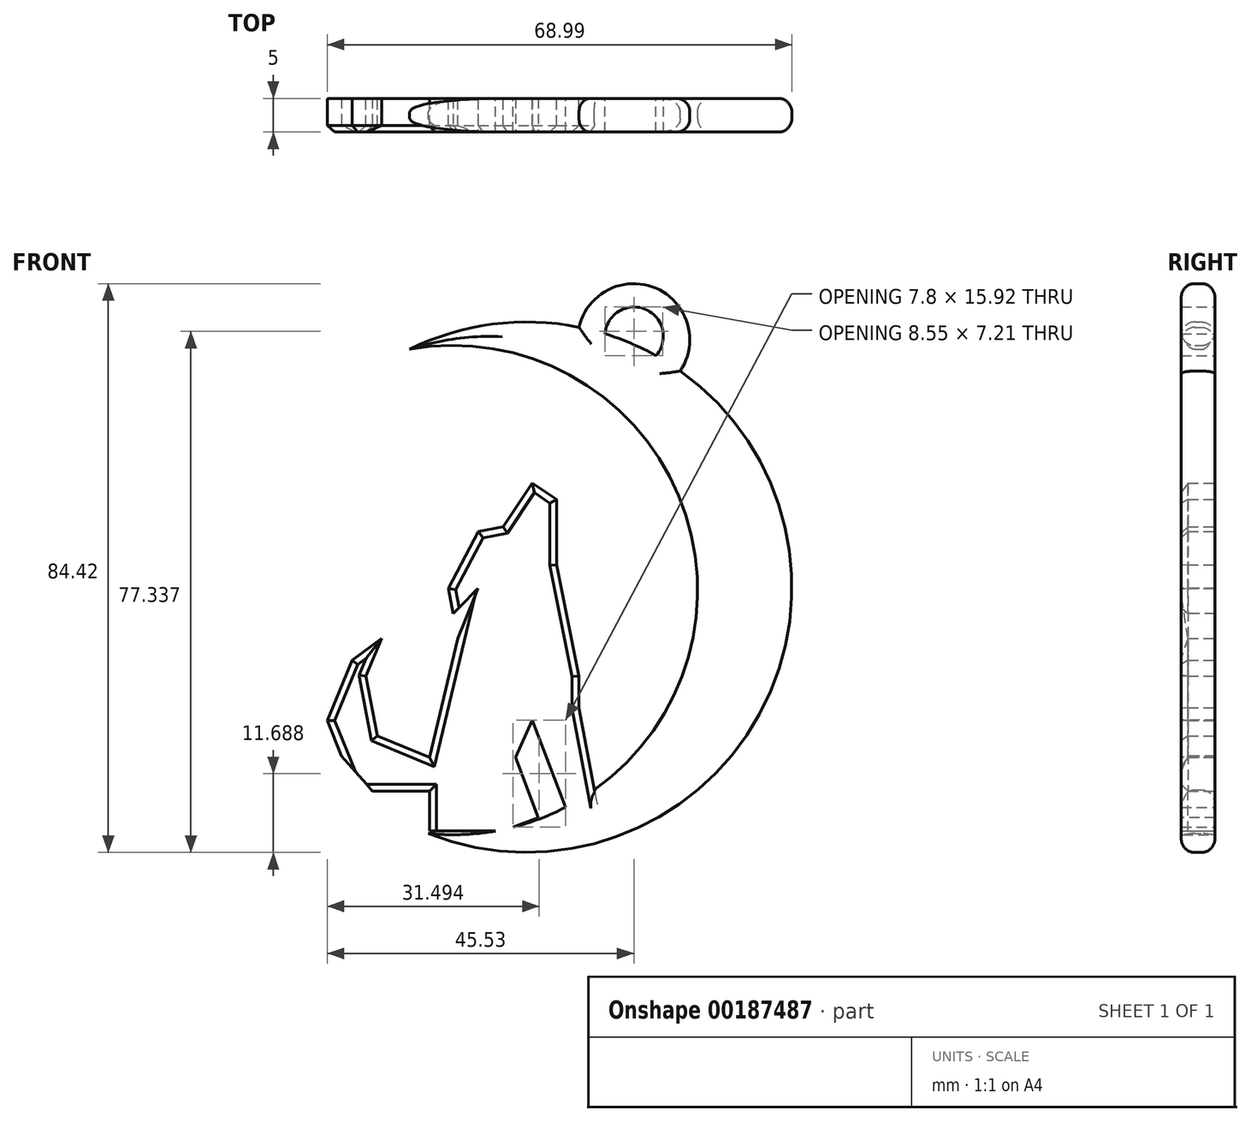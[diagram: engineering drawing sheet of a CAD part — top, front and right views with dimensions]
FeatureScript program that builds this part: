
annotation { "Feature Type Name" : "Feature", "Feature Type Description" : "" }
export const myFeature = defineFeature(function(context is Context, id is Id, definition is map)
    precondition{}
    {
        {
            var Q0;
            Q0=qCreatedBy(makeId("Front.planeOp"),FACE);
            var sketch = newSketch(context, id + "F0", { "sketchPlane" : qUnion([Q0])});
            skArc(sketch, "E0", {"start": v(-15.44, -36.36) * mm, "mid": v(33.72, -18.63) * mm, "end": v(21.95, 32.3) * mm});
            skArc(sketch, "E1", {"start": v(-15.44, -36.36) * mm, "mid": v(24.5, 1.2) * mm, "end": v(-18.25, 35.51) * mm});
            skArc(sketch, "E2", {"start": v(21.95, 32.3) * mm, "mid": v(18.35, 44.58) * mm, "end": v(6.93, 38.8) * mm});
            skArc(sketch, "E3", {"start": v(18.35, 34.57) * mm, "mid": v(16.81, 41.44) * mm, "end": v(10.78, 37.81) * mm});
            skPoint(sketch, "E3.startSnap0", {"position": v(18.35, 44.58) * mm});
            skArc(sketch, "E4.trimOffspring", {"start": v(6.93, 38.8) * mm, "mid": v(-5.93, 39.24) * mm, "end": v(-18.25, 35.51) * mm});
            skArc(sketch, "E5.trimOffspring", {"start": v(18.35, 34.57) * mm, "mid": v(14.65, 36.4) * mm, "end": v(10.78, 37.81) * mm});
            skSolve(sketch);
        }
        {
            var Q0;
            Q0=makeQuery(id+"F0.imprint","IMPRINT",FACE,{"disambiguationData":[TD([[makeQuery(id+"F0.imprint","IMPRINT",EDGE,{"derivedFrom":sQuery(id+"F0.wireOp",EDGE,"E0")}),1.0]])]});
            extrude(context, id + "F1", {"entities" : qUnion([Q0]), "depth" : 5 * mm});
        }
        {
            var Q0;
            Q0=qCreatedBy(makeId("Front.planeOp"),FACE);
            var sketch = newSketch(context, id + "F2", { "sketchPlane" : qUnion([Q0])});
            skLineSegment(sketch, "E6", {"start": v(-4.33, 9.14) * mm, "end": v(0, 15.63) * mm});
            skLineSegment(sketch, "E7", {"start": v(0, 15.63) * mm, "end": v(3.6, 13.23) * mm});
            skLineSegment(sketch, "E8", {"start": v(3.6, 13.23) * mm, "end": v(3.6, 3.54) * mm});
            skLineSegment(sketch, "E9", {"start": v(3.6, 3.54) * mm, "end": v(6.88, -12.98) * mm});
            skLineSegment(sketch, "E10", {"start": v(6.88, -12.98) * mm, "end": v(6.88, -17.7) * mm});
            skLineSegment(sketch, "E11", {"start": v(6.88, -17.7) * mm, "end": v(9.24, -30.08) * mm});
            skLineSegment(sketch, "E12", {"start": v(-4.33, 9.14) * mm, "end": v(-8, 8.44) * mm});
            skLineSegment(sketch, "E13", {"start": v(-8, 8.44) * mm, "end": v(-12.46, 0) * mm});
            skLineSegment(sketch, "E14", {"start": v(-12.46, 0) * mm, "end": v(-11.06, -7.37) * mm});
            skLineSegment(sketch, "E15", {"start": v(-11.06, -7.37) * mm, "end": v(-8, 0) * mm});
            skLineSegment(sketch, "E16", {"start": v(-11.06, -7.37) * mm, "end": v(-15.24, -25.07) * mm});
            skLineSegment(sketch, "E17", {"start": v(-15.24, -25.07) * mm, "end": v(-23, -21.86) * mm});
            skLineSegment(sketch, "E18", {"start": v(-23, -21.86) * mm, "end": v(-24.7, -12.98) * mm});
            skLineSegment(sketch, "E19", {"start": v(-24.7, -12.98) * mm, "end": v(-22.38, -7.37) * mm});
            skLineSegment(sketch, "E20", {"start": v(-22.38, -7.37) * mm, "end": v(-26.75, -10.62) * mm});
            skLineSegment(sketch, "E21", {"start": v(-26.75, -10.62) * mm, "end": v(-30.47, -19.61) * mm});
            skLineSegment(sketch, "E22", {"start": v(-30.47, -19.61) * mm, "end": v(-26.16, -30.08) * mm});
            skLineSegment(sketch, "E23", {"start": v(-26.16, -30.08) * mm, "end": v(-15.24, -30.08) * mm});
            skLineSegment(sketch, "E24", {"start": v(-15.24, -30.08) * mm, "end": v(-15.24, -35.98) * mm});
            skLineSegment(sketch, "E25", {"start": v(3.04, -19.61) * mm, "end": v(5.45, -32.27) * mm});
            skLineSegment(sketch, "E26", {"start": v(5.45, -32.27) * mm, "end": v(9.24, -30.08) * mm});
            skLineSegment(sketch, "E27", {"start": v(3.04, -19.61) * mm, "end": v(0.78, -25.07) * mm});
            skLineSegment(sketch, "E28", {"start": v(0.78, -25.07) * mm, "end": v(-1.3, -30.08) * mm});
            skLineSegment(sketch, "E29", {"start": v(-1.3, -30.08) * mm, "end": v(0.78, -30.94) * mm});
            skLineSegment(sketch, "E30", {"start": v(0.78, -30.94) * mm, "end": v(3.04, -31.88) * mm});
            skLineSegment(sketch, "E31", {"start": v(-15.24, -35.98) * mm, "end": v(-4.33, -35.98) * mm});
            skLineSegment(sketch, "E32", {"start": v(-4.33, -35.98) * mm, "end": v(5.45, -32.27) * mm});
            skSolve(sketch);
        }
        {
            var Q0;
            Q0=makeQuery(id+"F2.imprint","IMPRINT",FACE,{"disambiguationData":[TD([[makeQuery(id+"F2.imprint","IMPRINT",EDGE,{"derivedFrom":sQuery(id+"F2.wireOp",EDGE,"E6")}),-1.0]])]});
            extrude(context, id + "F3", {"entities" : qUnion([Q0]), "operationType" : NewBodyOperationType.ADD, "depth" : 5 * mm});
        }
        {
            var Q0;
            Q0=makeQuery(id+"F3.boolean.opBoolean","MERGE",FACE,{"derivedFrom":[makeQuery(id+"F1.opExtrude","CAP_FACE",FACE,{"disambiguationData":[OSD([sQuery(id+"F0.wireOp",EDGE,"E0"),sQuery(id+"F0.wireOp",EDGE,"E1"),sQuery(id+"F0.wireOp",EDGE,"E2"),sQuery(id+"F0.wireOp",EDGE,"E3"),sQuery(id+"F0.wireOp",EDGE,"E4.trimOffspring"),sQuery(id+"F0.wireOp",EDGE,"E5.trimOffspring")])],"isStart":false}),makeQuery(id+"F3.opExtrude","CAP_FACE",FACE,{"disambiguationData":[OSD([sQuery(id+"F2.wireOp",EDGE,"E6"),sQuery(id+"F2.wireOp",EDGE,"E7"),sQuery(id+"F2.wireOp",EDGE,"E8"),sQuery(id+"F2.wireOp",EDGE,"E9"),sQuery(id+"F2.wireOp",EDGE,"E10"),sQuery(id+"F2.wireOp",EDGE,"E11"),sQuery(id+"F2.wireOp",EDGE,"E12"),sQuery(id+"F2.wireOp",EDGE,"E13"),sQuery(id+"F2.wireOp",EDGE,"E14"),sQuery(id+"F2.wireOp",EDGE,"E16"),sQuery(id+"F2.wireOp",EDGE,"E17"),sQuery(id+"F2.wireOp",EDGE,"E18"),sQuery(id+"F2.wireOp",EDGE,"E19"),sQuery(id+"F2.wireOp",EDGE,"E20"),sQuery(id+"F2.wireOp",EDGE,"E21"),sQuery(id+"F2.wireOp",EDGE,"E22"),sQuery(id+"F2.wireOp",EDGE,"E23"),sQuery(id+"F2.wireOp",EDGE,"E24"),sQuery(id+"F2.wireOp",EDGE,"E26"),sQuery(id+"F2.wireOp",EDGE,"E31"),sQuery(id+"F2.wireOp",EDGE,"E32")])],"isStart":false})]});
            var sketch = newSketch(context, id + "F4", { "sketchPlane" : qUnion([Q0])});
            skLineSegment(sketch, "E33", {"start": v(-11.76, -3.69) * mm, "end": v(-8.11, 0) * mm});
            skLineSegment(sketch, "E34", {"start": v(-8.11, 0) * mm, "end": v(-11.06, -7.37) * mm});
            skLineSegment(sketch, "E35", {"start": v(-11.06, -7.37) * mm, "end": v(-11.76, -3.69) * mm});
            skLineSegment(sketch, "E36", {"start": v(4.92, -32.47) * mm, "end": v(0, -19.51) * mm});
            skLineSegment(sketch, "E37", {"start": v(0, -19.51) * mm, "end": v(-2.5, -25.07) * mm});
            skLineSegment(sketch, "E38", {"start": v(-2.5, -25.07) * mm, "end": v(0, -31.67) * mm});
            skLineSegment(sketch, "E39", {"start": v(0, -31.67) * mm, "end": v(0.97, -34.22) * mm});
            skLineSegment(sketch, "E40", {"start": v(0.97, -34.22) * mm, "end": v(4.92, -32.47) * mm});
            skLineSegment(sketch, "E41", {"start": v(-28.31, -24.85) * mm, "end": v(-23.74, -30.08) * mm});
            skLineSegment(sketch, "E42", {"start": v(-23.74, -30.08) * mm, "end": v(-26.16, -30.08) * mm});
            skLineSegment(sketch, "E43", {"start": v(-26.16, -30.08) * mm, "end": v(-28.31, -24.85) * mm});
            skSolve(sketch);
        }
        {
            var Q0;
            Q0=makeQuery(id+"F4.imprint","IMPRINT",FACE,{"disambiguationData":[TD([[makeQuery(id+"F4.imprint","IMPRINT",EDGE,{"derivedFrom":sQuery(id+"F4.wireOp",EDGE,"E33")}),-1.0]])]});
            var Q1;
            {var subQ5=sQuery(id+"F4.wireOp",EDGE,"E36");Q1=makeQuery(id+"F4.imprint","IMPRINT",FACE,{"disambiguationData":[TD([[makeQuery(id+"F4.imprint","IMPRINT",EDGE,{"derivedFrom":subQ5}),1.0]])]});}
            var Q2;
            Q2=makeQuery(id+"F4.imprint","IMPRINT",FACE,{"disambiguationData":[TD([[makeQuery(id+"F4.imprint","IMPRINT",EDGE,{"derivedFrom":sQuery(id+"F4.wireOp",EDGE,"E41")}),-1.0]])]});
            extrude(context, id + "F5", {"entities" : qUnion([Q0, Q1, Q2]), "operationType" : NewBodyOperationType.REMOVE, "oppositeDirection" : true, "depth" : 5 * mm});
        }
        {
            var Q0;
            {var subQ1=sQuery(id+"F0.wireOp",EDGE,"E4.trimOffspring");var subQ2=sQuery(id+"F0.wireOp",EDGE,"E1");Q0=makeQuery(id+"F3.boolean.opBoolean","SPLIT",EDGE,{"disambiguationData":[TD([makeQuery(id+"F1.opExtrude","SWEPT_FACE",FACE,{"disambiguationData":[OSD([subQ1])]})])],"derivedFrom":makeQuery(id+"F1.opExtrude","CAP_EDGE",EDGE,{"disambiguationData":[OSD([subQ2])],"isStart":false})});}
            var Q1;
            Q1=makeQuery(id+"F1.opExtrude","CAP_EDGE",EDGE,{"disambiguationData":[OSD([sQuery(id+"F0.wireOp",EDGE,"E4.trimOffspring")])],"isStart":false});
            var Q2;
            Q2=makeQuery(id+"F1.opExtrude","CAP_EDGE",EDGE,{"disambiguationData":[OSD([sQuery(id+"F0.wireOp",EDGE,"E0")])],"isStart":false});
            var Q3;
            Q3=makeQuery(id+"F1.opExtrude","CAP_EDGE",EDGE,{"disambiguationData":[OSD([sQuery(id+"F0.wireOp",EDGE,"E2")])],"isStart":false});
            var Q4;
            Q4=makeQuery(id+"F1.opExtrude","CAP_EDGE",EDGE,{"disambiguationData":[OSD([sQuery(id+"F0.wireOp",EDGE,"E0")])],"isStart":true});
            var Q5;
            {var subQ0=sQuery(id+"F0.wireOp",EDGE,"E4.trimOffspring");var subQ1=sQuery(id+"F0.wireOp",EDGE,"E1");Q5=makeQuery(id+"F3.boolean.opBoolean","SPLIT",EDGE,{"disambiguationData":[TD([makeQuery(id+"F1.opExtrude","SWEPT_FACE",FACE,{"disambiguationData":[OSD([subQ0])]})])],"derivedFrom":makeQuery(id+"F1.opExtrude","CAP_EDGE",EDGE,{"disambiguationData":[OSD([subQ1])],"isStart":true})});}
            var Q6;
            Q6=makeQuery(id+"F1.opExtrude","CAP_EDGE",EDGE,{"disambiguationData":[OSD([sQuery(id+"F0.wireOp",EDGE,"E2")])],"isStart":true});
            var Q7;
            Q7=makeQuery(id+"F1.opExtrude","CAP_EDGE",EDGE,{"disambiguationData":[OSD([sQuery(id+"F0.wireOp",EDGE,"E4.trimOffspring")])],"isStart":true});
            fillet(context, id + "F6", {"entities" : qUnion([Q0, Q1, Q2, Q3, Q4, Q5, Q6, Q7]), "radius" : 2 * mm, "tangentPropagation" : true, "allowEdgeOverflow" : false});
        }
        {
            var Q0;
            Q0=makeQuery(id+"F3.opExtrude","CAP_EDGE",EDGE,{"disambiguationData":[OSD([sQuery(id+"F2.wireOp",EDGE,"E6")])],"isStart":false});
            var Q1;
            Q1=makeQuery(id+"F3.opExtrude","CAP_EDGE",EDGE,{"disambiguationData":[OSD([sQuery(id+"F2.wireOp",EDGE,"E7")])],"isStart":false});
            var Q2;
            Q2=makeQuery(id+"F3.opExtrude","CAP_EDGE",EDGE,{"disambiguationData":[OSD([sQuery(id+"F2.wireOp",EDGE,"E8")])],"isStart":false});
            var Q3;
            Q3=makeQuery(id+"F3.opExtrude","CAP_EDGE",EDGE,{"disambiguationData":[OSD([sQuery(id+"F2.wireOp",EDGE,"E9")])],"isStart":false});
            var Q4;
            Q4=makeQuery(id+"F3.opExtrude","CAP_EDGE",EDGE,{"disambiguationData":[OSD([sQuery(id+"F2.wireOp",EDGE,"E11")])],"isStart":false});
            var Q5;
            Q5=makeQuery(id+"F3.opExtrude","CAP_EDGE",EDGE,{"disambiguationData":[OSD([sQuery(id+"F2.wireOp",EDGE,"E10")])],"isStart":false});
            var Q6;
            Q6=makeQuery(id+"F3.opExtrude","CAP_EDGE",EDGE,{"disambiguationData":[OSD([sQuery(id+"F2.wireOp",EDGE,"E12")])],"isStart":false});
            var Q7;
            Q7=makeQuery(id+"F3.opExtrude","CAP_EDGE",EDGE,{"disambiguationData":[OSD([sQuery(id+"F2.wireOp",EDGE,"E13")])],"isStart":false});
            var Q8;
            Q8=makeQuery(id+"F3.opExtrude","CAP_EDGE",EDGE,{"disambiguationData":[OSD([sQuery(id+"F2.wireOp",EDGE,"E14")])],"isStart":false});
            var Q9;
            Q9=makeQuery(id+"F5.boolean.opBoolean","COPY",EDGE,{"derivedFrom":makeQuery(id+"F5.opExtrude","CAP_EDGE",EDGE,{"disambiguationData":[OSD([sQuery(id+"F4.wireOp",EDGE,"E34")])],"isStart":true})});
            var Q10;
            Q10=makeQuery(id+"F5.boolean.opBoolean","COPY",EDGE,{"derivedFrom":makeQuery(id+"F5.opExtrude","CAP_EDGE",EDGE,{"disambiguationData":[OSD([sQuery(id+"F4.wireOp",EDGE,"E33")])],"isStart":true})});
            var Q11;
            Q11=makeQuery(id+"F3.opExtrude","CAP_EDGE",EDGE,{"disambiguationData":[OSD([sQuery(id+"F2.wireOp",EDGE,"E16")])],"isStart":false});
            var Q12;
            Q12=makeQuery(id+"F3.opExtrude","CAP_EDGE",EDGE,{"disambiguationData":[OSD([sQuery(id+"F2.wireOp",EDGE,"E17")])],"isStart":false});
            var Q13;
            Q13=makeQuery(id+"F3.opExtrude","CAP_EDGE",EDGE,{"disambiguationData":[OSD([sQuery(id+"F2.wireOp",EDGE,"E18")])],"isStart":false});
            var Q14;
            Q14=makeQuery(id+"F3.opExtrude","CAP_EDGE",EDGE,{"disambiguationData":[OSD([sQuery(id+"F2.wireOp",EDGE,"E19")])],"isStart":false});
            var Q15;
            Q15=makeQuery(id+"F3.opExtrude","CAP_EDGE",EDGE,{"disambiguationData":[OSD([sQuery(id+"F2.wireOp",EDGE,"E20")])],"isStart":false});
            var Q16;
            Q16=makeQuery(id+"F3.opExtrude","CAP_EDGE",EDGE,{"disambiguationData":[OSD([sQuery(id+"F2.wireOp",EDGE,"E21")])],"isStart":false});
            var Q17;
            Q17=makeQuery(id+"F3.opExtrude","CAP_EDGE",EDGE,{"disambiguationData":[OSD([sQuery(id+"F2.wireOp",EDGE,"E22")])],"isStart":false});
            var Q18;
            Q18=makeQuery(id+"F5.boolean.opBoolean","COPY",EDGE,{"derivedFrom":makeQuery(id+"F5.opExtrude","CAP_EDGE",EDGE,{"disambiguationData":[OSD([sQuery(id+"F4.wireOp",EDGE,"E41")])],"isStart":true})});
            var Q19;
            Q19=makeQuery(id+"F3.opExtrude","CAP_EDGE",EDGE,{"disambiguationData":[OSD([sQuery(id+"F2.wireOp",EDGE,"E23")])],"isStart":false});
            var Q20;
            Q20=makeQuery(id+"F3.opExtrude","CAP_EDGE",EDGE,{"disambiguationData":[OSD([sQuery(id+"F2.wireOp",EDGE,"E24")])],"isStart":false});
            var Q21;
            Q21=makeQuery(id+"F5.boolean.opBoolean","COPY",EDGE,{"derivedFrom":makeQuery(id+"F5.opExtrude","CAP_EDGE",EDGE,{"disambiguationData":[OSD([sQuery(id+"F4.wireOp",EDGE,"E38"),sQuery(id+"F4.wireOp",EDGE,"E39")])],"isStart":true})});
            var Q22;
            Q22=makeQuery(id+"F5.boolean.opBoolean","COPY",EDGE,{"derivedFrom":makeQuery(id+"F5.opExtrude","CAP_EDGE",EDGE,{"disambiguationData":[OSD([sQuery(id+"F4.wireOp",EDGE,"E37")])],"isStart":true})});
            var Q23;
            Q23=makeQuery(id+"F5.boolean.opBoolean","COPY",EDGE,{"derivedFrom":makeQuery(id+"F5.opExtrude","CAP_EDGE",EDGE,{"disambiguationData":[OSD([sQuery(id+"F4.wireOp",EDGE,"E36")])],"isStart":true})});
            chamfer(context, id + "F7", {"entities" : qUnion([Q0, Q1, Q2, Q3, Q4, Q5, Q6, Q7, Q8, Q9, Q10, Q11, Q12, Q13, Q14, Q15, Q16, Q17, Q18, Q19, Q20, Q21, Q22, Q23]), "width" : 1 * mm, "tangentPropagation" : true});
        }
    });
